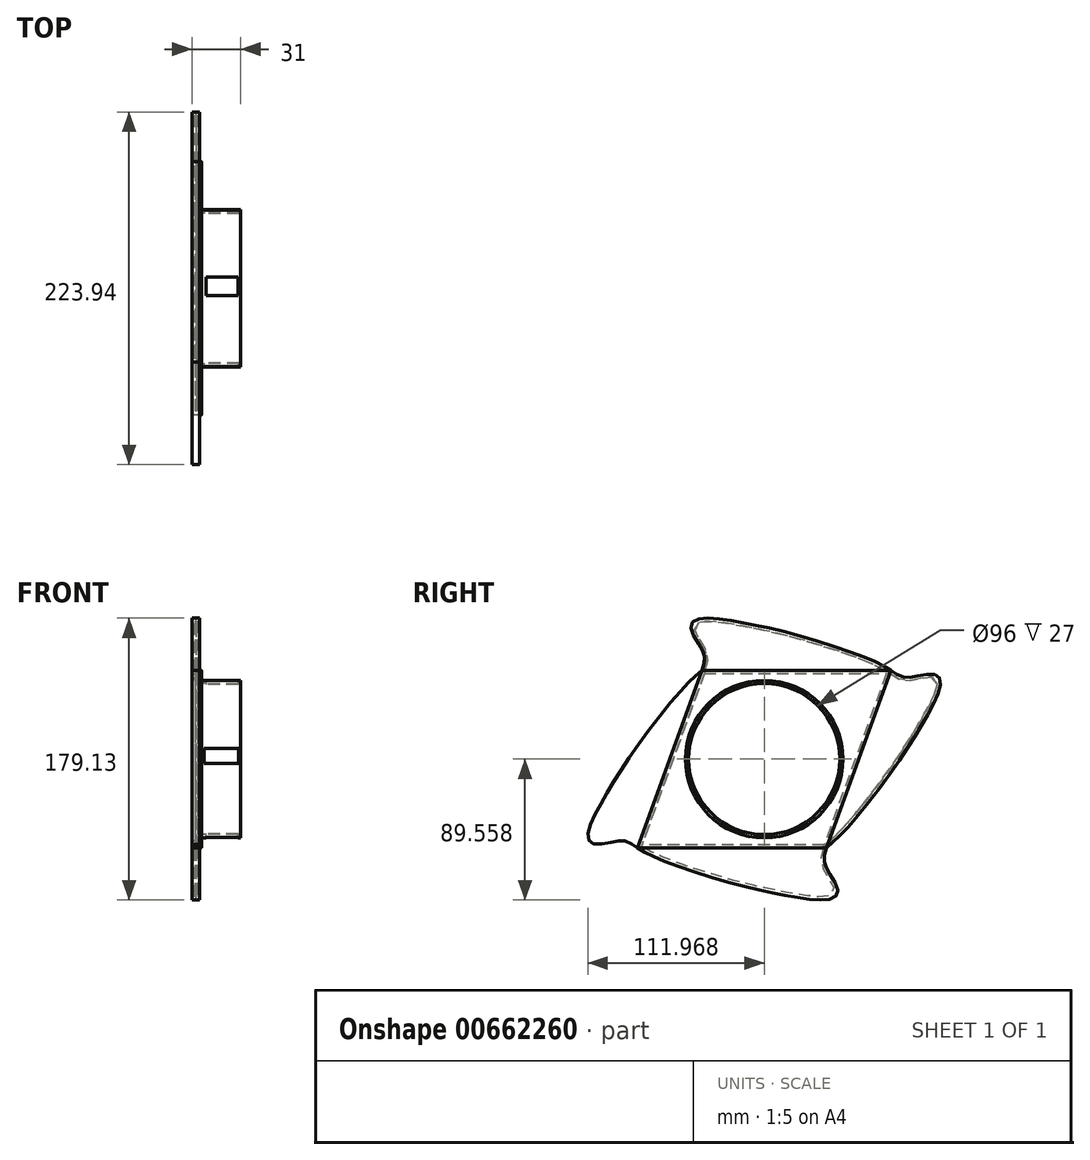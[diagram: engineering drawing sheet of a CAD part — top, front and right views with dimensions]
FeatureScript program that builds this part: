
annotation { "Feature Type Name" : "Feature", "Feature Type Description" : "" }
export const myFeature = defineFeature(function(context is Context, id is Id, definition is map)
    precondition{}
    {
        {
            var Q0;
            Q0=qCreatedBy(makeId("Right.planeOp"),FACE);
            var sketch = newSketch(context, id + "F0", { "sketchPlane" : qUnion([Q0])});
            skLineSegment(sketch, "E0", {"start": v(-49.72, 53.03) * mm, "end": v(-90.76, -59.73) * mm});
            skLineSegment(sketch, "E1", {"start": v(-90.76, -59.73) * mm, "end": v(29.24, -59.73) * mm});
            skLineSegment(sketch, "E2", {"start": v(29.24, -59.73) * mm, "end": v(70.28, 53.03) * mm});
            skLineSegment(sketch, "E3", {"start": v(70.28, 53.03) * mm, "end": v(-49.72, 53.03) * mm});
            skFitSpline(sketch, "E4", {"points": [v(-49.72, 53.03) * mm, v(-48.33, 61.82) * mm, v(-52.1, 70.03) * mm, v(-56.89, 81.67) * mm, v(-50.21, 85.95) * mm, v(-27.8, 83.9) * mm, v(6.26, 76.54) * mm, v(54.35, 60.96) * mm, v(70.28, 53.03) * mm], "startDerivative": vector(30.63, 101.59) * mm, "endDerivative": vector(110.84, -65.33) * mm});
            skFitSpline(sketch, "E5", {"points": [v(-90.76, -59.73) * mm, v(-98.55, -55.43) * mm, v(-107.55, -56.15) * mm, v(-120.13, -56.68) * mm, v(-121.86, -48.94) * mm, v(-112.27, -28.58) * mm, v(-93.7, 0.9) * mm, v(-62.62, 40.77) * mm, v(-49.72, 53.03) * mm], "startDerivative": vector(-84.98, 63.53) * mm, "endDerivative": vector(99.3, 81.81) * mm});
            skFitSpline(sketch, "E6", {"points": [v(70.28, 53.03) * mm, v(78.07, 48.72) * mm, v(87.08, 49.45) * mm, v(99.65, 49.97) * mm, v(101.39, 42.24) * mm, v(91.8, 21.87) * mm, v(73.23, -7.61) * mm, v(42.15, -47.47) * mm, v(29.24, -59.73) * mm], "startDerivative": vector(84.98, -63.53) * mm, "endDerivative": vector(-99.3, -81.81) * mm});
            skLineSegment(sketch, "E7", {"start": v(-90.76, -59.74) * mm, "end": v(29.24, -59.74) * mm});
            skFitSpline(sketch, "E8", {"points": [v(29.24, -59.73) * mm, v(27.86, -68.53) * mm, v(31.62, -76.74) * mm, v(36.41, -88.38) * mm, v(29.74, -92.66) * mm, v(7.32, -90.6) * mm, v(-26.73, -83.24) * mm, v(-74.82, -67.67) * mm, v(-90.76, -59.73) * mm], "startDerivative": vector(-30.63, -101.59) * mm, "endDerivative": vector(-110.84, 65.33) * mm});
            skSolve(sketch);
        }
        {
            var Q0;
            Q0 = qSketchRegion(id + "F0", true);
            extrude(context, id + "F1", {"entities" : qUnion([Q0]), "depth" : 5 * mm, "offsetDistance" : 25 * mm});
        }
        {
            var Q0;
            {var subQ0=sQuery(id+"F0.wireOp",EDGE,"E1");Q0=makeQuery(id+"F0.imprint","IMPRINT",FACE,{"disambiguationData":[TD([[makeQuery(id+"F0.imprint","IMPRINT",EDGE,{"derivedFrom":subQ0}),1.0]])]});}
            extrude(context, id + "F2", {"entities" : qUnion([Q0]), "operationType" : NewBodyOperationType.ADD, "depth" : 6 * mm, "offsetDistance" : 25 * mm});
        }
        {
            var Q0;
            Q0=makeQuery(id+"F2.opExtrude","CAP_FACE",FACE,{"disambiguationData":[OSD([sQuery(id+"F0.wireOp",EDGE,"E0"),sQuery(id+"F0.wireOp",EDGE,"E1"),sQuery(id+"F0.wireOp",EDGE,"E2"),sQuery(id+"F0.wireOp",EDGE,"E3")])],"isStart":false});
            fillet(context, id + "F3", {"entities" : qUnion([Q0]), "radius" : 0.09 * mm, "tangentPropagation" : true, "allowEdgeOverflow" : false});
        }
        {
            var Q0;
            Q0=makeQuery(id+"F2.opExtrude","CAP_FACE",FACE,{"disambiguationData":[OSD([sQuery(id+"F0.wireOp",EDGE,"E0"),sQuery(id+"F0.wireOp",EDGE,"E1"),sQuery(id+"F0.wireOp",EDGE,"E2"),sQuery(id+"F0.wireOp",EDGE,"E3")])],"isStart":false});
            var sketch = newSketch(context, id + "F4", { "sketchPlane" : qUnion([Q0])});
            skCircle(sketch, "E9", {"center": v(-10.24, -3.36) * mm, "radius": 50 * mm});
            skSolve(sketch);
        }
        {
            var Q0;
            Q0 = qSketchRegion(id + "F4", true);
            extrude(context, id + "F5", {"entities" : qUnion([Q0]), "operationType" : NewBodyOperationType.ADD, "depth" : 25 * mm, "offsetDistance" : 25 * mm});
        }
        {
            var Q0;
            Q0=makeQuery(id+"F5.opExtrude","CAP_FACE",FACE,{"disambiguationData":[OSD([sQuery(id+"F4.wireOp",EDGE,"E9")])],"isStart":false});
            shell(context, id + "F6", {"entities" : qUnion([Q0]), "thickness" : 2 * mm});
        }
        {
            var Q0;
            Q0=qCreatedBy(makeId("Front.planeOp"),FACE);
            var sketch = newSketch(context, id + "F7", { "sketchPlane" : qUnion([Q0])});
            skLineSegment(sketch, "E10.bottom", {"start": v(7.66, -6.05) * mm, "end": v(29.66, -6.05) * mm});
            skLineSegment(sketch, "E10.top", {"start": v(7.66, 3.28) * mm, "end": v(29.66, 3.28) * mm});
            skLineSegment(sketch, "E10.left", {"start": v(7.66, -6.05) * mm, "end": v(7.66, 3.28) * mm});
            skLineSegment(sketch, "E10.right", {"start": v(29.66, -6.05) * mm, "end": v(29.66, 3.28) * mm});
            skSolve(sketch);
        }
        {
            var Q0;
            Q0=makeQuery(id+"F7.imprint","IMPRINT",FACE,{"disambiguationData":[TD([[makeQuery(id+"F7.imprint","IMPRINT",EDGE,{"derivedFrom":sQuery(id+"F7.wireOp",EDGE,"E10.bottom")}),1.0]])]});
            extrude(context, id + "F8", {"entities" : qUnion([Q0]), "operationType" : NewBodyOperationType.REMOVE, "oppositeDirection" : true, "depth" : 76.2 * mm, "offsetDistance" : 25 * mm});
        }
        {
            var Q0;
            Q0 = qSketchRegion(id + "F7", true);
            extrude(context, id + "F9", {"entities" : qUnion([Q0]), "operationType" : NewBodyOperationType.REMOVE, "depth" : 93.7 * mm, "offsetDistance" : 25 * mm});
        }
        {
            var Q0;
            Q0=qCreatedBy(makeId("Top.planeOp"),FACE);
            var sketch = newSketch(context, id + "F10", { "sketchPlane" : qUnion([Q0])});
            skLineSegment(sketch, "E11.bottom", {"start": v(8.87, -14.83) * mm, "end": v(29.19, -14.83) * mm});
            skLineSegment(sketch, "E11.top", {"start": v(8.87, -3.05) * mm, "end": v(29.19, -3.05) * mm});
            skLineSegment(sketch, "E11.left", {"start": v(8.87, -14.83) * mm, "end": v(8.87, -3.05) * mm});
            skLineSegment(sketch, "E11.right", {"start": v(29.19, -14.83) * mm, "end": v(29.19, -3.05) * mm});
            skSolve(sketch);
        }
        {
            var Q0;
            Q0=makeQuery(id+"F10.imprint","IMPRINT",FACE,{"disambiguationData":[TD([[makeQuery(id+"F10.imprint","IMPRINT",EDGE,{"derivedFrom":sQuery(id+"F10.wireOp",EDGE,"E11.bottom")}),1.0]])]});
            extrude(context, id + "F11", {"entities" : qUnion([Q0]), "operationType" : NewBodyOperationType.REMOVE, "oppositeDirection" : true, "depth" : 69.1 * mm, "offsetDistance" : 25 * mm});
        }
        {
            var Q0;
            Q0 = qSketchRegion(id + "F10", true);
            extrude(context, id + "F12", {"entities" : qUnion([Q0]), "operationType" : NewBodyOperationType.REMOVE, "depth" : 68 * mm, "offsetDistance" : 25 * mm});
        }
    });
